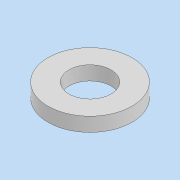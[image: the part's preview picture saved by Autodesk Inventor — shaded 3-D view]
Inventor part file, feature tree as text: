
AUTODESK INVENTOR PART (.ipt)
format: ipt  version: 2022 (Build 260153000, 153)  size: 88,064 bytes
history: native  units: mm
features: extrude x1, sketch x1
ambient origin geometry x8: Origin, YZ Plane, XZ Plane, XY Plane, X Axis, Y Axis, Z Axis, Center Point
bodies: Solide1 (feature_tree)
feature tree (2):
  extrude  "Extrusion1"  Depth=3.0mm
  sketch  "Esquisse1"
